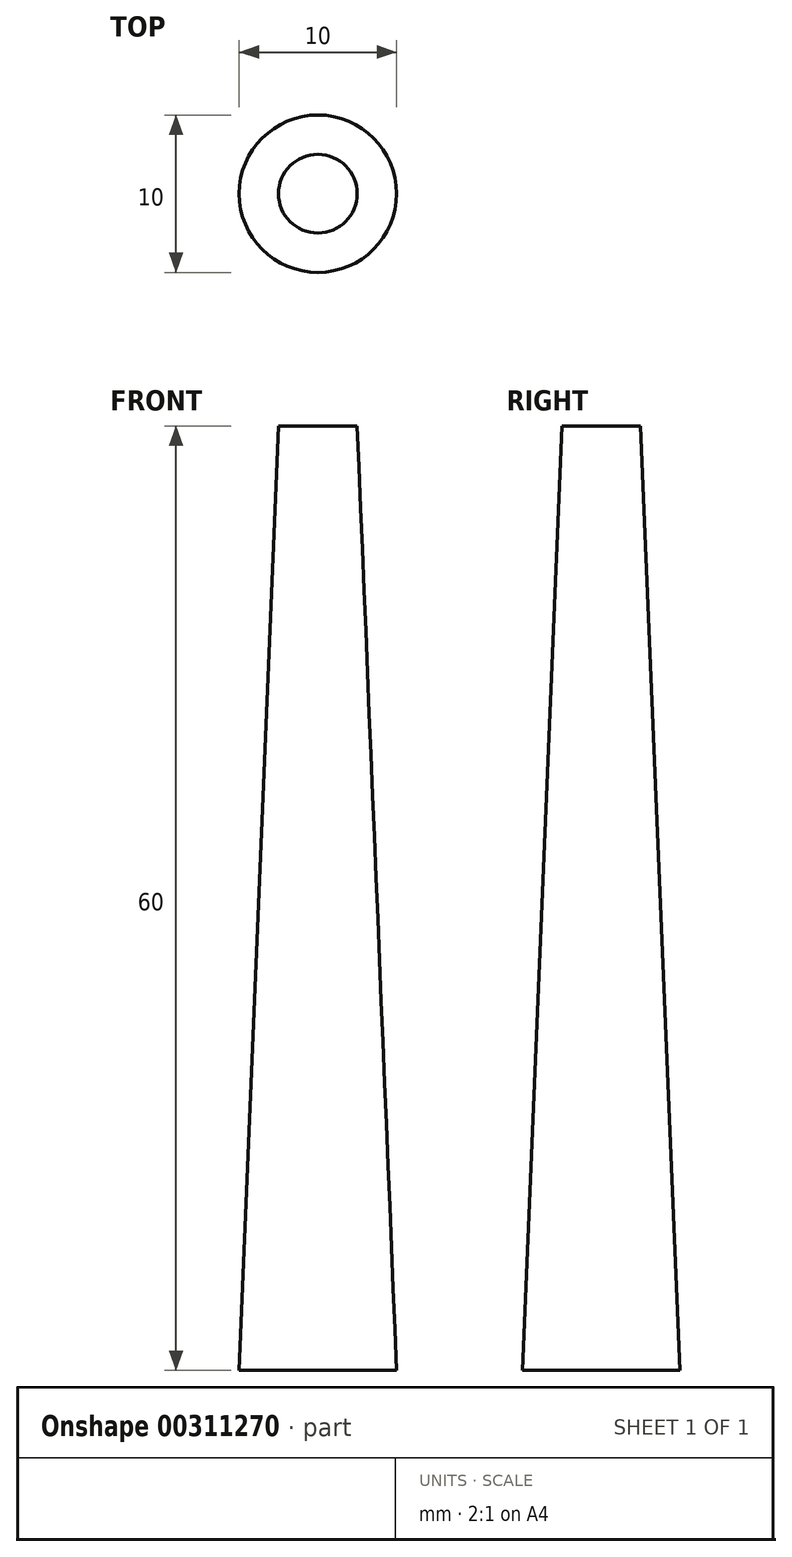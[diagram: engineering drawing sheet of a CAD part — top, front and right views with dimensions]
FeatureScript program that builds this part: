
annotation { "Feature Type Name" : "Feature", "Feature Type Description" : "" }
export const myFeature = defineFeature(function(context is Context, id is Id, definition is map)
    precondition{}
    {
        {
            var Q0;
            Q0=qCreatedBy(makeId("Top.planeOp"),FACE);
            var sketch = newSketch(context, id + "F0", { "sketchPlane" : qUnion([Q0])});
            skCircle(sketch, "E0", {"center": v(0, 0) * mm, "radius": 5 * mm});
            skSolve(sketch);
        }
        {
            var Q0;
            Q0=qCreatedBy(makeId("Top.planeOp"),FACE);
            cPlane(context, id + "F1", {"entities" : qUnion([Q0]), "cplaneType" : CPlaneType.OFFSET, "offset" : 60 * mm, "width" : 150 * mm, "height" : 150 * mm});
        }
        {
            var Q0;
            Q0=qCreatedBy(id+"F1.planeOp",FACE);
            var sketch = newSketch(context, id + "F2", { "sketchPlane" : qUnion([Q0])});
            skCircle(sketch, "E1", {"center": v(0, 0) * mm, "radius": 2.5 * mm});
            skSolve(sketch);
        }
        {
            var Q0;
            Q0 = qSketchRegion(id + "F0", true);
            var Q1;
            Q1 = qSketchRegion(id + "F2", true);
            loft(context, id + "F3", {"sheetProfilesArray" : [{ "sheetProfileEntities" : qUnion([Q0]) }, { "sheetProfileEntities" : qUnion([Q1]) }]});
        }
    });
